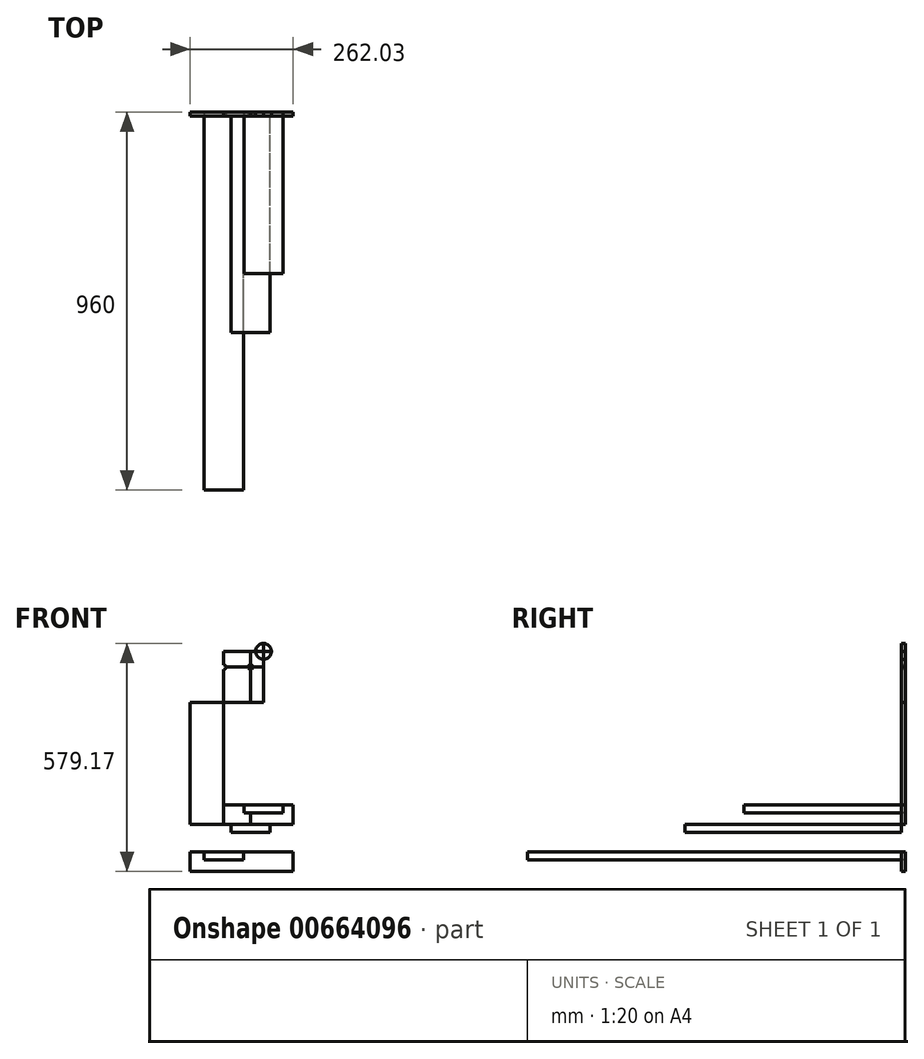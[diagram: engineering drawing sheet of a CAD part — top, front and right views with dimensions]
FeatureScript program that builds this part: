
annotation { "Feature Type Name" : "Feature", "Feature Type Description" : "" }
export const myFeature = defineFeature(function(context is Context, id is Id, definition is map)
    precondition{}
    {
        {
            var Q0;
            Q0=qCreatedBy(makeId("Front.planeOp"),FACE);
            var sketch = newSketch(context, id + "F0", { "sketchPlane" : qUnion([Q0])});
            skLineSegment(sketch, "E0", {"start": v(-110.46, 42.26) * mm, "end": v(55.36, 42.26) * mm});
            skLineSegment(sketch, "E1", {"start": v(54.25, 2.26) * mm, "end": v(-122.21, 2.26) * mm});
            skLineSegment(sketch, "E2", {"start": v(23.68, 70.59) * mm, "end": v(23.68, -347.74) * mm});
            skLineSegment(sketch, "E3.bottom", {"start": v(-269.42, 126.88) * mm, "end": v(368.87, 126.88) * mm});
            skLineSegment(sketch, "E3.top", {"start": v(-269.42, -88.04) * mm, "end": v(368.87, -88.04) * mm});
            skLineSegment(sketch, "E3.left", {"start": v(-269.42, 126.88) * mm, "end": v(-269.42, -88.04) * mm});
            skLineSegment(sketch, "E3.right", {"start": v(368.87, 126.88) * mm, "end": v(368.87, -88.04) * mm});
            skCircle(sketch, "E4", {"center": v(23.68, 42.26) * mm, "radius": 20 * mm});
            skLineSegment(sketch, "E5", {"start": v(-9.32, 88.68) * mm, "end": v(-9.32, -397.74) * mm});
            skLineSegment(sketch, "E6", {"start": v(-77.32, 77.18) * mm, "end": v(-77.32, -467.74) * mm});
            skCircle(sketch, "E7", {"center": v(-9.32, 2.26) * mm, "radius": 6 * mm});
            skCircle(sketch, "E8", {"center": v(-77.32, 2.26) * mm, "radius": 6 * mm});
            skLineSegment(sketch, "E9", {"start": v(-162.45, -347.74) * mm, "end": v(109.8, -347.74) * mm});
            skLineSegment(sketch, "E10", {"start": v(158.77, -397.74) * mm, "end": v(-165.2, -397.74) * mm});
            skLineSegment(sketch, "E11", {"start": v(162.78, -467.74) * mm, "end": v(-247.23, -467.74) * mm});
            skLineSegment(sketch, "E12.bottom", {"start": v(-26.32, -347.74) * mm, "end": v(73.68, -347.74) * mm});
            skLineSegment(sketch, "E12.top", {"start": v(-26.32, -367.74) * mm, "end": v(73.68, -367.74) * mm});
            skLineSegment(sketch, "E12.left", {"start": v(-26.32, -347.74) * mm, "end": v(-26.32, -367.74) * mm});
            skLineSegment(sketch, "E12.right", {"start": v(73.68, -347.74) * mm, "end": v(73.68, -367.74) * mm});
            skLineSegment(sketch, "E13.bottom", {"start": v(-59.32, -397.74) * mm, "end": v(40.68, -397.74) * mm});
            skLineSegment(sketch, "E13.top", {"start": v(-59.32, -417.74) * mm, "end": v(40.68, -417.74) * mm});
            skLineSegment(sketch, "E13.left", {"start": v(-59.32, -397.74) * mm, "end": v(-59.32, -417.74) * mm});
            skLineSegment(sketch, "E13.right", {"start": v(40.68, -397.74) * mm, "end": v(40.68, -417.74) * mm});
            skLineSegment(sketch, "E14.bottom", {"start": v(-127.32, -467.74) * mm, "end": v(-27.32, -467.74) * mm});
            skLineSegment(sketch, "E14.top", {"start": v(-127.32, -487.74) * mm, "end": v(-27.32, -487.74) * mm});
            skLineSegment(sketch, "E14.left", {"start": v(-127.32, -467.74) * mm, "end": v(-127.32, -487.74) * mm});
            skLineSegment(sketch, "E14.right", {"start": v(-27.32, -467.74) * mm, "end": v(-27.32, -487.74) * mm});
            skLineSegment(sketch, "E15.bottom", {"start": v(-162.68, -88.04) * mm, "end": v(99.35, -88.04) * mm});
            skLineSegment(sketch, "E15.top", {"start": v(-162.68, -516.9) * mm, "end": v(99.35, -516.9) * mm});
            skLineSegment(sketch, "E15.left", {"start": v(-162.68, -88.04) * mm, "end": v(-162.68, -516.9) * mm});
            skLineSegment(sketch, "E15.right", {"start": v(99.35, -88.04) * mm, "end": v(99.35, -516.9) * mm});
            skSolve(sketch);
        }
        {
            var Q0;
            Q0=makeQuery(id+"F0.imprint","IMPRINT",FACE,{"disambiguationData":[TD([[makeQuery(id+"F0.imprint","IMPRINT",EDGE,{"derivedFrom":sQuery(id+"F0.wireOp",EDGE,"E14.top")}),-1.0]])]});
            var Q1;
            {var subQ3=sQuery(id+"F0.wireOp",EDGE,"E2");var subQ5=sQuery(id+"F0.wireOp",EDGE,"E12.bottom");var subQ6=makeQuery(id+"F0.imprint","INTERSECT",VERTEX,{"derivedFrom":[subQ3,subQ5]});Q1=makeQuery(id+"F0.imprint","IMPRINT",FACE,{"disambiguationData":[TD([[makeQuery(id+"F0.imprint","IMPRINT",EDGE,{"disambiguationData":[TD([[subQ6,1.0]])],"derivedFrom":subQ3}),1.0]])]});}
            var Q2;
            {var subQ0=sQuery(id+"F0.wireOp",EDGE,"E6");var subQ1=makeQuery(id+"F0.imprint","INTERSECT",VERTEX,{"derivedFrom":[subQ0,sQuery(id+"F0.wireOp",EDGE,"E9")]});Q2=makeQuery(id+"F0.imprint","IMPRINT",FACE,{"disambiguationData":[TD([[makeQuery(id+"F0.imprint","IMPRINT",EDGE,{"disambiguationData":[TD([[subQ1,1.0]])],"derivedFrom":subQ0}),-1.0]])]});}
            var Q3;
            {var subQ0=sQuery(id+"F0.wireOp",EDGE,"E14.bottom");var subQ1=sQuery(id+"F0.wireOp",EDGE,"E6");var subQ2=makeQuery(id+"F0.imprint","INTERSECT",VERTEX,{"derivedFrom":[subQ1,subQ0]});Q3=makeQuery(id+"F0.imprint","IMPRINT",FACE,{"disambiguationData":[TD([[makeQuery(id+"F0.imprint","IMPRINT",EDGE,{"disambiguationData":[TD([[subQ2,1.0]])],"derivedFrom":subQ1}),-1.0]])]});}
            var Q4;
            {var subQ5=sQuery(id+"F0.wireOp",EDGE,"E12.right");Q4=makeQuery(id+"F0.imprint","IMPRINT",FACE,{"disambiguationData":[TD([[makeQuery(id+"F0.imprint","IMPRINT",EDGE,{"derivedFrom":subQ5}),1.0]])]});}
            var Q5;
            Q5=makeQuery(id+"F0.imprint","IMPRINT",FACE,{"disambiguationData":[TD([[makeQuery(id+"F0.imprint","IMPRINT",EDGE,{"derivedFrom":sQuery(id+"F0.wireOp",EDGE,"E13.top")}),-1.0]])]});
            var Q6;
            Q6=makeQuery(id+"F0.imprint","IMPRINT",FACE,{"disambiguationData":[TD([[makeQuery(id+"F0.imprint","IMPRINT",EDGE,{"derivedFrom":sQuery(id+"F0.wireOp",EDGE,"E3.bottom")}),-1.0]])]});
            var Q7;
            {var subQ0=sQuery(id+"F0.wireOp",EDGE,"E6");var subQ1=sQuery(id+"F0.wireOp",EDGE,"E0");var subQ2=makeQuery(id+"F0.imprint","INTERSECT",VERTEX,{"derivedFrom":[subQ1,subQ0]});Q7=makeQuery(id+"F0.imprint","IMPRINT",FACE,{"disambiguationData":[TD([[makeQuery(id+"F0.imprint","IMPRINT",EDGE,{"disambiguationData":[TD([[subQ2,-1.0]])],"derivedFrom":subQ1}),-1.0]])]});}
            var Q8;
            {var subQ1=sQuery(id+"F0.wireOp",EDGE,"E0");var subQ7=sQuery(id+"F0.wireOp",EDGE,"E5");var subQ8=makeQuery(id+"F0.imprint","INTERSECT",VERTEX,{"derivedFrom":[subQ1,subQ7]});Q8=makeQuery(id+"F0.imprint","IMPRINT",FACE,{"disambiguationData":[TD([[makeQuery(id+"F0.imprint","IMPRINT",EDGE,{"disambiguationData":[TD([[subQ8,-1.0]])],"derivedFrom":subQ1}),-1.0]])]});}
            var Q9;
            {var subQ1=sQuery(id+"F0.wireOp",EDGE,"E1");var subQ7=sQuery(id+"F0.wireOp",EDGE,"E2");var subQ8=makeQuery(id+"F0.imprint","INTERSECT",VERTEX,{"derivedFrom":[subQ1,subQ7]});Q9=makeQuery(id+"F0.imprint","IMPRINT",FACE,{"disambiguationData":[TD([[makeQuery(id+"F0.imprint","IMPRINT",EDGE,{"disambiguationData":[TD([[subQ8,-1.0]])],"derivedFrom":subQ1}),1.0]])]});}
            var Q10;
            {var subQ0=sQuery(id+"F0.wireOp",EDGE,"E7");var subQ1=sQuery(id+"F0.wireOp",EDGE,"E1");var subQ2=makeQuery(id+"F0.imprint","INTERSECT",VERTEX,{"disambiguationData":[OD(1.0)],"derivedFrom":[subQ1,subQ0]});Q10=makeQuery(id+"F0.imprint","IMPRINT",FACE,{"disambiguationData":[TD([[makeQuery(id+"F0.imprint","IMPRINT",EDGE,{"disambiguationData":[TD([[subQ2,-1.0]])],"derivedFrom":subQ1}),1.0]])]});}
            var Q11;
            {var subQ5=sQuery(id+"F0.wireOp",EDGE,"E15.bottom");var subQ7=sQuery(id+"F0.wireOp",EDGE,"E5");var subQ9=makeQuery(id+"F0.imprint","INTERSECT",VERTEX,{"derivedFrom":[subQ7,subQ5]});Q11=makeQuery(id+"F0.imprint","IMPRINT",FACE,{"disambiguationData":[TD([[makeQuery(id+"F0.imprint","IMPRINT",EDGE,{"disambiguationData":[TD([[subQ9,-1.0]])],"derivedFrom":subQ7}),-1.0]])]});}
            var Q12;
            {var subQ0=sQuery(id+"F0.wireOp",EDGE,"E12.bottom");var subQ1=sQuery(id+"F0.wireOp",EDGE,"E2");var subQ2=makeQuery(id+"F0.imprint","INTERSECT",VERTEX,{"derivedFrom":[subQ1,subQ0]});Q12=makeQuery(id+"F0.imprint","IMPRINT",FACE,{"disambiguationData":[TD([[makeQuery(id+"F0.imprint","IMPRINT",EDGE,{"disambiguationData":[TD([[subQ2,1.0]])],"derivedFrom":subQ1}),-1.0]])]});}
            var Q13;
            {var subQ7=sQuery(id+"F0.wireOp",EDGE,"E12.left");Q13=makeQuery(id+"F0.imprint","IMPRINT",FACE,{"disambiguationData":[TD([[makeQuery(id+"F0.imprint","IMPRINT",EDGE,{"derivedFrom":subQ7}),-1.0]])]});}
            extrude(context, id + "F1", {"entities" : qUnion([Q0, Q1, Q2, Q3, Q4, Q5, Q6, Q7, Q8, Q9, Q10, Q11, Q12, Q13]), "depth" : -10 * mm, "offsetDistance" : 25 * mm});
        }
        {
            var Q0;
            {var subQ0=sQuery(id+"F0.wireOp",EDGE,"E12.right");Q0=makeQuery(id+"F0.imprint","IMPRINT",FACE,{"disambiguationData":[TD([[makeQuery(id+"F0.imprint","IMPRINT",EDGE,{"derivedFrom":subQ0}),-1.0]])]});}
            var Q1;
            {var subQ5=sQuery(id+"F0.wireOp",EDGE,"E12.left");Q1=makeQuery(id+"F0.imprint","IMPRINT",FACE,{"disambiguationData":[TD([[makeQuery(id+"F0.imprint","IMPRINT",EDGE,{"derivedFrom":subQ5}),1.0]])]});}
            extrude(context, id + "F2", {"entities" : qUnion([Q0, Q1]), "flatOperationType" : FlatOperationType.REMOVE, "depth" : 400 * mm, "offsetDistance" : 25 * mm, "domain" : OperationDomain.MODEL});
        }
        {
            var Q0;
            Q0=makeQuery(id+"F0.imprint","IMPRINT",FACE,{"disambiguationData":[TD([[makeQuery(id+"F0.imprint","IMPRINT",EDGE,{"derivedFrom":sQuery(id+"F0.wireOp",EDGE,"E13.top")}),1.0]])]});
            extrude(context, id + "F3", {"entities" : qUnion([Q0]), "depth" : 550 * mm, "offsetDistance" : 25 * mm});
        }
        {
            var Q0;
            Q0=makeQuery(id+"F0.imprint","IMPRINT",FACE,{"disambiguationData":[TD([[makeQuery(id+"F0.imprint","IMPRINT",EDGE,{"derivedFrom":sQuery(id+"F0.wireOp",EDGE,"E14.top")}),1.0]])]});
            extrude(context, id + "F4", {"entities" : qUnion([Q0]), "depth" : 950 * mm, "offsetDistance" : 25 * mm});
        }
    });
